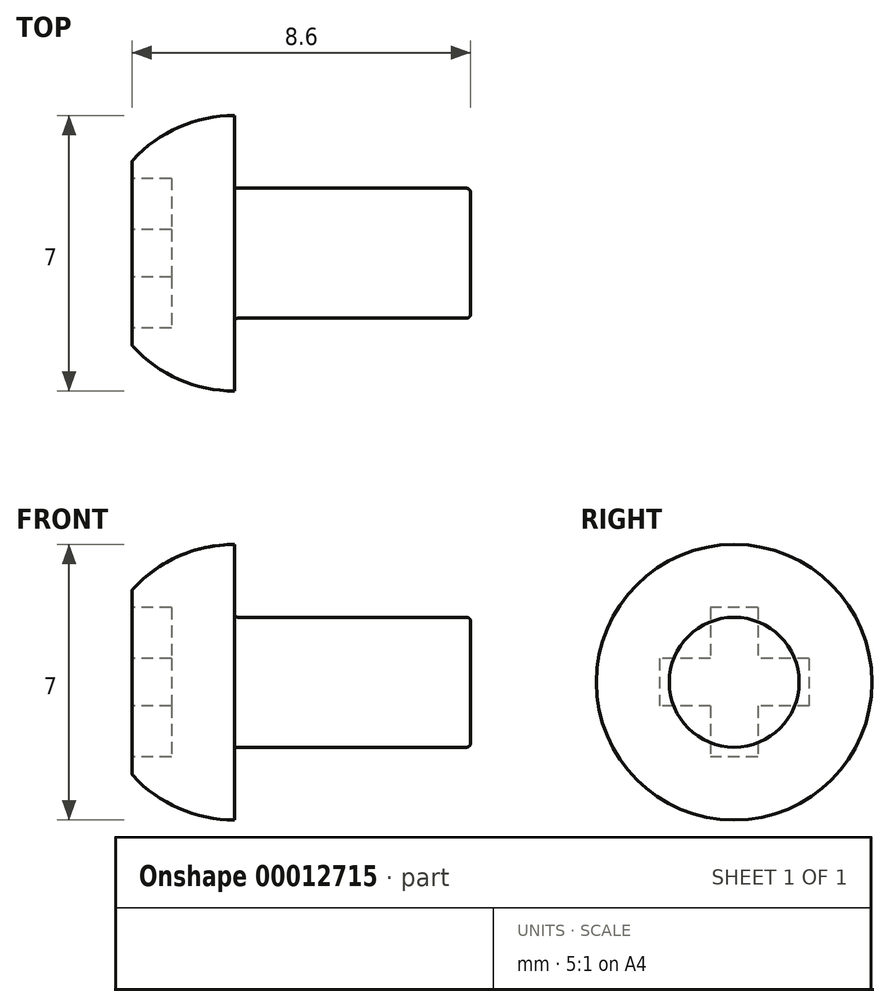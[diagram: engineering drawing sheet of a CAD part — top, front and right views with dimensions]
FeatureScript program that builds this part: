
annotation { "Feature Type Name" : "Feature", "Feature Type Description" : "" }
export const myFeature = defineFeature(function(context is Context, id is Id, definition is map)
    precondition{}
    {
        {
            var Q0;
            Q0=qCreatedBy(makeId("Top.planeOp"),FACE);
            var sketch = newSketch(context, id + "F0", { "sketchPlane" : qUnion([Q0])});
            skPoint(sketch, "E0", {"position": v(2.6, 0) * mm});
            skLineSegment(sketch, "E1", {"start": v(0, 0) * mm, "end": v(8.6, 0) * mm});
            skLineSegment(sketch, "E2", {"start": v(8.6, 0) * mm, "end": v(8.6, 1.65) * mm});
            skLineSegment(sketch, "E3", {"start": v(8.6, 1.65) * mm, "end": v(2.6, 1.65) * mm});
            skLineSegment(sketch, "E4", {"start": v(2.6, 1.65) * mm, "end": v(2.6, 3.5) * mm});
            skLineSegment(sketch, "E5", {"start": v(0, 0) * mm, "end": v(0, 2.34) * mm});
            skPoint(sketch, "E6", {"position": v(0, 2.34) * mm});
            skPoint(sketch, "E7", {"position": v(2.6, 3.5) * mm});
            skCircle(sketch, "E8", {"center": v(2.6, 0) * mm, "radius": 3.5 * mm});
            skSolve(sketch);
        }
        {
            var Q0;
            {var subQ2=sQuery(id+"F0.wireOp",EDGE,"E4");Q0=makeQuery(id+"F0.imprint","IMPRINT",FACE,{"disambiguationData":[TD([[makeQuery(id+"F0.imprint","IMPRINT",EDGE,{"derivedFrom":subQ2}),1.0]])]});}
            var Q1;
            {var subQ5=sQuery(id+"F0.wireOp",EDGE,"E2");Q1=makeQuery(id+"F0.imprint","IMPRINT",FACE,{"disambiguationData":[TD([[makeQuery(id+"F0.imprint","IMPRINT",EDGE,{"derivedFrom":subQ5}),1.0]])]});}
            var Q2;
            Q2=sQuery(id+"F0.wireOp",EDGE,"E1");
            revolve(context, id + "F1", {"entities" : qUnion([Q0, Q1]), "axis" : qUnion([Q2]), "revolveType" : RevolveType.FULL});
        }
        {
            var Q0;
            Q0=makeQuery(id+"F1.opRevolve","SWEPT_EDGE",EDGE,{"disambiguationData":[OSD([sQuery(id+"F0.wireOp",EDGE,"E3"),sQuery(id+"F0.wireOp",EDGE,"E4")])]});
            var Q1;
            Q1=makeQuery(id+"F1.opRevolve","SWEPT_EDGE",EDGE,{"disambiguationData":[OSD([sQuery(id+"F0.wireOp",EDGE,"E2"),sQuery(id+"F0.wireOp",EDGE,"E3")])]});
            var Q2;
            Q2=makeQuery(id+"F1.opRevolve","SWEPT_EDGE",EDGE,{"disambiguationData":[OSD([sQuery(id+"F0.wireOp",EDGE,"E5"),sQuery(id+"F0.wireOp",EDGE,"E8")])]});
            fillet(context, id + "F2", {"entities" : qUnion([Q0, Q1, Q2]), "radius" : 0.1 * mm, "tangentPropagation" : true, "allowEdgeOverflow" : false});
        }
        {
            var Q0;
            Q0=makeQuery(id+"F1.opRevolve","SWEPT_FACE",FACE,{"disambiguationData":[OSD([sQuery(id+"F0.wireOp",EDGE,"E5")])]});
            var sketch = newSketch(context, id + "F3", { "sketchPlane" : qUnion([Q0])});
            skLineSegment(sketch, "E9.rect.bottom", {"start": v(-1.9, 0.6) * mm, "end": v(1.9, 0.6) * mm});
            skLineSegment(sketch, "E9.rect.top", {"start": v(-1.9, -0.6) * mm, "end": v(1.9, -0.6) * mm});
            skLineSegment(sketch, "E9.rect.left", {"start": v(-1.9, 0.6) * mm, "end": v(-1.9, -0.6) * mm});
            skLineSegment(sketch, "E9.rect.right", {"start": v(1.9, 0.6) * mm, "end": v(1.9, -0.6) * mm});
            skPoint(sketch, "E9.rect.middle", {"position": v(0, 0) * mm});
            skLineSegment(sketch, "E10.rect.bottom", {"start": v(-0.6, 1.9) * mm, "end": v(0.6, 1.9) * mm});
            skLineSegment(sketch, "E10.rect.top", {"start": v(-0.6, -1.9) * mm, "end": v(0.6, -1.9) * mm});
            skLineSegment(sketch, "E10.rect.left", {"start": v(-0.6, 1.9) * mm, "end": v(-0.6, -1.9) * mm});
            skLineSegment(sketch, "E10.rect.right", {"start": v(0.6, 1.9) * mm, "end": v(0.6, -1.9) * mm});
            skSolve(sketch);
        }
        {
            var Q0;
            Q0 = qSketchRegion(id + "F3", true);
            extrude(context, id + "F4", {"entities" : qUnion([Q0]), "operationType" : NewBodyOperationType.REMOVE, "oppositeDirection" : true, "depth" : 1 * mm});
        }
    });
